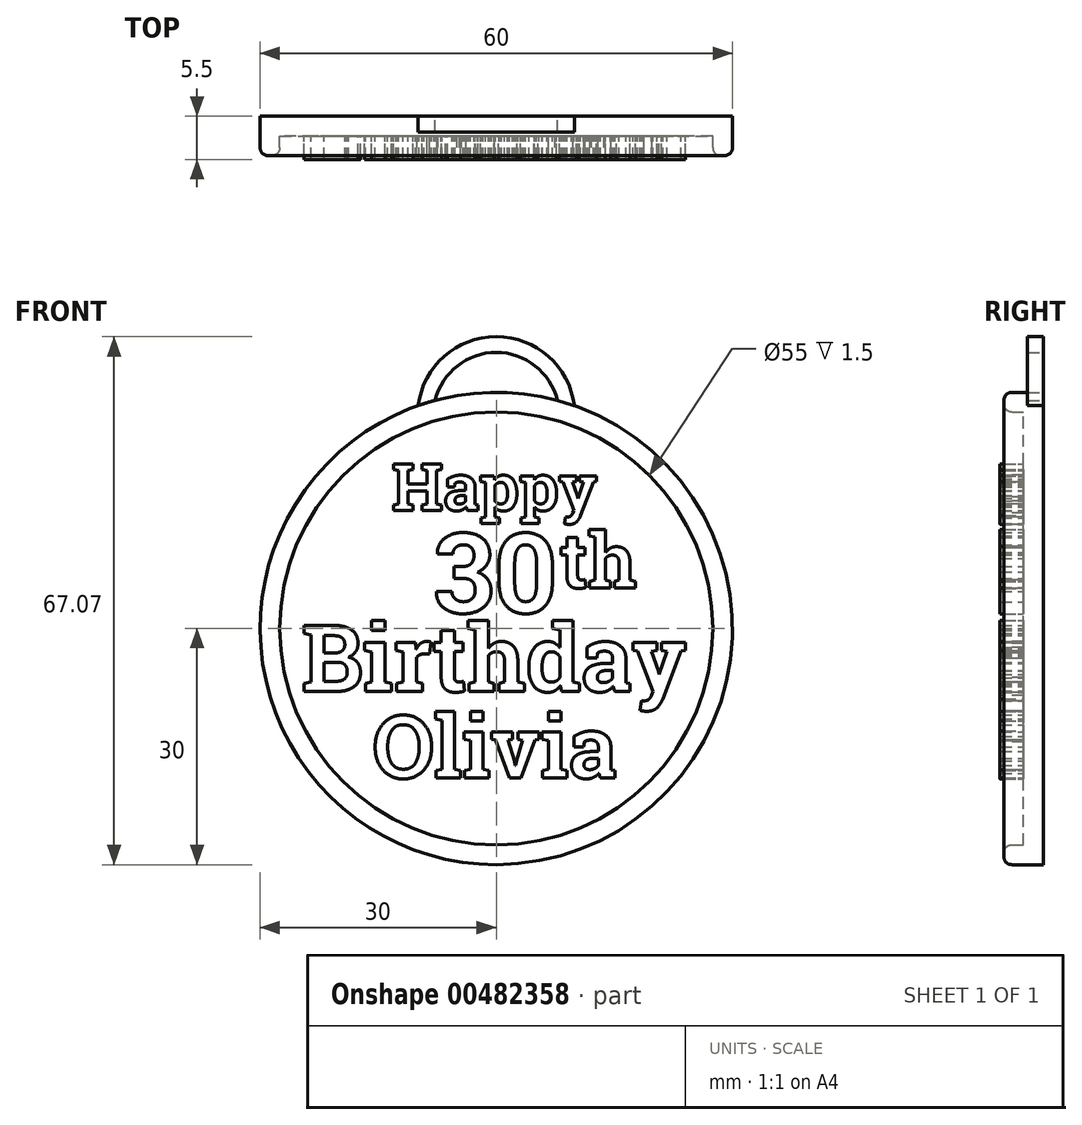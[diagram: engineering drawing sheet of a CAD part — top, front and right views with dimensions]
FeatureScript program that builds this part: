
annotation { "Feature Type Name" : "Feature", "Feature Type Description" : "" }
export const myFeature = defineFeature(function(context is Context, id is Id, definition is map)
    precondition{}
    {
        {
            var Q0;
            Q0=qCreatedBy(makeId("Front.planeOp"),FACE);
            var sketch = newSketch(context, id + "F0", { "sketchPlane" : qUnion([Q0])});
            skCircle(sketch, "E0", {"center": v(0, 0) * mm, "radius": 30 * mm});
            skSolve(sketch);
        }
        {
            var Q0;
            Q0 = qSketchRegion(id + "F0", true);
            extrude(context, id + "F1", {"entities" : qUnion([Q0]), "depth" : 5 * mm});
        }
        {
            var Q0;
            Q0=makeQuery(id+"F1.opExtrude","CAP_FACE",FACE,{"disambiguationData":[OSD([sQuery(id+"F0.wireOp",EDGE,"E0")])],"isStart":false});
            shell(context, id + "F2", {"entities" : qUnion([Q0]), "thickness" : 2.5 * mm});
        }
        {
            var Q0;
            {var subQ0=sQuery(id+"F0.wireOp",EDGE,"E0");Q0=makeQuery(id+"F2.opShell","OFFSET_FACE",FACE,{"disambiguationData":[OSD([subQ0]),TDD([makeQuery(id+"F1.opExtrude","CAP_FACE",FACE,{"disambiguationData":[OSD([subQ0])],"isStart":true})])]});}
            var sketch = newSketch(context, id + "F3", { "sketchPlane" : qUnion([Q0])});
            skText(sketch, "E1", { "text": "30", "fontName": "RobotoSlab-Bold.ttf"});
            skText(sketch, "E2", { "text": "Happy", "fontName": "RobotoSlab-Bold.ttf"});
            skText(sketch, "E3", { "text": "Birthday", "fontName": "RobotoSlab-Bold.ttf"});
            skText(sketch, "E4", { "text": "th", "fontName": "RobotoSlab-Bold.ttf"});
            skText(sketch, "E5", { "text": "Olivia", "fontName": "RobotoSlab-Bold.ttf"});
            const initialGuessF3  = {"E1": [-0.008, 0.002, 1, 0, 0.01017], "E2": [-0.01325, 0.015, 1, 0, 0.006], "E3": [-0.02475, -0.008, 1, 0, 0.0085], "E4": [0.008, 0.00517, 1, 0, 0.007], "E5": [-0.01574, -0.019, 1, 0, 0.008]};
            skSetInitialGuess(sketch, initialGuessF3);
            skSolve(sketch);
        }
        {
            var Q0;
            Q0 = qSketchRegion(id + "F3", true);
            extrude(context, id + "F4", {"entities" : qUnion([Q0]), "operationType" : NewBodyOperationType.ADD, "depth" : 3 * mm});
        }
        {
            var Q0;
            Q0=qCreatedBy(makeId("Front.planeOp"),FACE);
            var sketch = newSketch(context, id + "F5", { "sketchPlane" : qUnion([Q0])});
            skArc(sketch, "E6", {"start": v(7.77, 28.98) * mm, "mid": v(0, 35.07) * mm, "end": v(-7.77, 28.98) * mm});
            skCircle(sketch, "E7", {"center": v(0, 0) * mm, "radius": 30 * mm, "construction": true});
            skArc(sketch, "E8.0", {"start": v(9.92, 28.31) * mm, "mid": v(0, 37.07) * mm, "end": v(-9.92, 28.31) * mm});
            skLineSegment(sketch, "E9", {"start": v(-9.92, 28.31) * mm, "end": v(-7.77, 28.98) * mm});
            skLineSegment(sketch, "E10", {"start": v(7.77, 28.98) * mm, "end": v(9.92, 28.31) * mm});
            skSolve(sketch);
        }
        {
            var Q0;
            Q0 = qSketchRegion(id + "F5", true);
            extrude(context, id + "F6", {"entities" : qUnion([Q0]), "operationType" : NewBodyOperationType.ADD, "depth" : 2 * mm});
        }
        {
            var Q0;
            {var subQ0=sQuery(id+"F0.wireOp",EDGE,"E0");Q0=makeQuery(id+"F2.opShell","OFFSET_EDGE",EDGE,{"disambiguationData":[OSD([subQ0]),TDD([makeQuery(id+"F1.opExtrude","CAP_EDGE",EDGE,{"disambiguationData":[OSD([subQ0])],"isStart":false})])]});}
            var Q1;
            Q1=makeQuery(id+"F1.opExtrude","CAP_EDGE",EDGE,{"disambiguationData":[OSD([sQuery(id+"F0.wireOp",EDGE,"E0")])],"isStart":false});
            fillet(context, id + "F7", {"entities" : qUnion([Q0, Q1]), "radius" : 1 * mm, "tangentPropagation" : true, "allowEdgeOverflow" : false});
        }
    });
